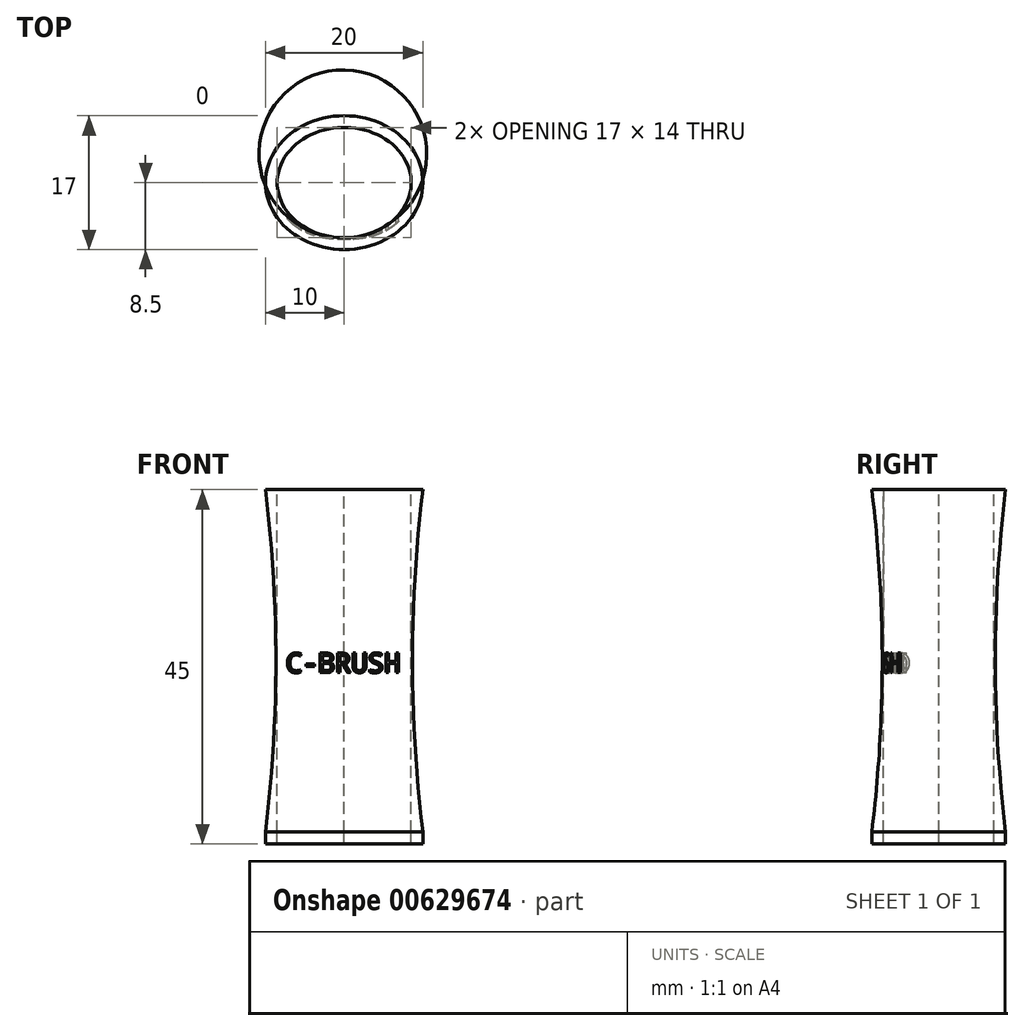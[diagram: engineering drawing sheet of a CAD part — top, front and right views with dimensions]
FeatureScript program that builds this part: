
annotation { "Feature Type Name" : "Feature", "Feature Type Description" : "" }
export const myFeature = defineFeature(function(context is Context, id is Id, definition is map)
    precondition{}
    {
        {
            var Q0;
            Q0=qCreatedBy(makeId("Top.planeOp"),FACE);
            var sketch = newSketch(context, id + "F0", { "sketchPlane" : qUnion([Q0])});
            skEllipse(sketch, "E0", {"center": v(0, 0) * mm, "majorRadius": 10 * mm, "minorRadius": 8.5 * mm, "majorAxis": v(-1, 0)});
            skSolve(sketch);
        }
        {
            var Q0;
            Q0 = qSketchRegion(id + "F0", true);
            extrude(context, id + "F1", {"entities" : qUnion([Q0]), "depth" : 1.5 * mm, "offsetDistance" : 25 * mm});
        }
        {
            var Q0;
            Q0=makeQuery(id+"F1.opExtrude","CAP_FACE",FACE,{"disambiguationData":[OSD([sQuery(id+"F0.wireOp",EDGE,"E0")])],"isStart":false});
            var sketch = newSketch(context, id + "F2", { "sketchPlane" : qUnion([Q0])});
            skSolve(sketch);
        }
        {
            var Q0;
            Q0=qCreatedBy(makeId("Top.planeOp"),FACE);
            cPlane(context, id + "F3", {"entities" : qUnion([Q0]), "cplaneType" : CPlaneType.OFFSET, "offset" : 45 * mm, "width" : 150 * mm, "height" : 150 * mm});
        }
        {
            var Q0;
            Q0=qCreatedBy(id+"F3.planeOp",FACE);
            var sketch = newSketch(context, id + "F4", { "sketchPlane" : qUnion([Q0])});
            skEllipse(sketch, "E1", {"center": v(0, 0) * mm, "majorRadius": 10 * mm, "minorRadius": 8.5 * mm, "majorAxis": v(-1, 0)});
            skSolve(sketch);
        }
        {
            var Q0;
            Q0=qCreatedBy(makeId("Front.planeOp"),FACE);
            var sketch = newSketch(context, id + "F5", { "sketchPlane" : qUnion([Q0])});
            skLineSegment(sketch, "E2", {"start": v(0, 0) * mm, "end": v(0, 1.5) * mm, "construction": true});
            skLineSegment(sketch, "E3", {"start": v(0, 1.5) * mm, "end": v(-10, 1.5) * mm, "construction": true});
            skLineSegment(sketch, "E4", {"start": v(0, 1.5) * mm, "end": v(10, 1.5) * mm, "construction": true});
            skLineSegment(sketch, "E5", {"start": v(-10, 1.5) * mm, "end": v(-10, 45) * mm, "construction": true});
            skLineSegment(sketch, "E6", {"start": v(10, 1.5) * mm, "end": v(10, 45) * mm, "construction": true});
            skArc(sketch, "E7", {"start": v(-10, 1.5) * mm, "mid": v(-8.68, 23.25) * mm, "end": v(-10, 45) * mm});
            skArc(sketch, "E8", {"start": v(10, 45) * mm, "mid": v(8.68, 23.25) * mm, "end": v(10, 1.5) * mm});
            skSolve(sketch);
        }
        {
            var Q0;
            Q0=qCreatedBy(makeId("Right.planeOp"),FACE);
            var sketch = newSketch(context, id + "F6", { "sketchPlane" : qUnion([Q0])});
            skLineSegment(sketch, "E9", {"start": v(0, 0) * mm, "end": v(0, 1.5) * mm, "construction": true});
            skLineSegment(sketch, "E10", {"start": v(0, 1.5) * mm, "end": v(8.5, 1.5) * mm, "construction": true});
            skLineSegment(sketch, "E11", {"start": v(8.5, 1.5) * mm, "end": v(8.5, 45) * mm, "construction": true});
            skLineSegment(sketch, "E12", {"start": v(0, 1.5) * mm, "end": v(-8.5, 1.5) * mm, "construction": true});
            skLineSegment(sketch, "E13", {"start": v(-8.5, 1.5) * mm, "end": v(-8.5, 45) * mm, "construction": true});
            skArc(sketch, "E14", {"start": v(-8.5, 1.5) * mm, "mid": v(-7.18, 23.25) * mm, "end": v(-8.5, 45) * mm});
            skArc(sketch, "E15", {"start": v(8.5, 45) * mm, "mid": v(7.18, 23.25) * mm, "end": v(8.5, 1.5) * mm});
            skSolve(sketch);
        }
        {
            var Q0;
            Q0=makeQuery(id+"F2.imprint","IMPRINT",FACE,{"disambiguationData":[TD([[makeQuery(id+"F2.imprint","IMPRINT",EDGE,{"derivedFrom":makeQuery(id+"F1.opExtrude","CAP_EDGE",EDGE,{"disambiguationData":[OSD([sQuery(id+"F0.wireOp",EDGE,"E0")])],"isStart":false})}),1.0]])]});
            var Q1;
            Q1 = qSketchRegion(id + "F4", true);
            var Q2;
            Q2=sQuery(id+"F5.wireOp",EDGE,"E7");
            var Q3;
            Q3=sQuery(id+"F5.wireOp",EDGE,"E8");
            var Q4;
            Q4=sQuery(id+"F6.wireOp",EDGE,"E14");
            var Q5;
            Q5=sQuery(id+"F6.wireOp",EDGE,"E15");
            loft(context, id + "F7", {"addGuides" : true, "sheetProfilesArray" : [{ "sheetProfileEntities" : qUnion([Q0]) }, { "sheetProfileEntities" : qUnion([Q1]) }], "guidesArray" : [{ "guideEntities" : qUnion([Q2]), "guideDerivativeType" : LoftGuideDerivativeType.DEFAULT, "guideDerivativeMagnitude" : 1 }, { "guideEntities" : qUnion([Q3]), "guideDerivativeType" : LoftGuideDerivativeType.DEFAULT, "guideDerivativeMagnitude" : 1 }, { "guideEntities" : qUnion([Q4]), "guideDerivativeType" : LoftGuideDerivativeType.DEFAULT, "guideDerivativeMagnitude" : 1 }, { "guideEntities" : qUnion([Q5]), "guideDerivativeType" : LoftGuideDerivativeType.DEFAULT, "guideDerivativeMagnitude" : 1 }]});
        }
        {
            var Q0;
            Q0=qCreatedBy(makeId("Front.planeOp"),FACE);
            var sketch = newSketch(context, id + "F8", { "sketchPlane" : qUnion([Q0])});
            skText(sketch, "E16", { "text": "C-BRUSH", "fontName": "DroidSansMono.ttf"});
            const initialGuessF8  = {"E16": [-0.00744, 0.02175, 1, 0, 0.0025]};
            skSetInitialGuess(sketch, initialGuessF8);
            skSolve(sketch);
        }
        {
            var Q0;
            Q0 = qSketchRegion(id + "F8", true);
            extrude(context, id + "F9", {"entities" : qUnion([Q0]), "operationType" : NewBodyOperationType.REMOVE, "endBound" : BoundingType.THROUGH_ALL, "depth" : 25 * mm, "offsetDistance" : 25 * mm});
        }
        {
            var Q0;
            Q0=makeQuery(id+"F7.opLoft","CAP_FACE",FACE,{"disambiguationData":[OSD([makeQuery(id+"F4.imprint","IMPRINT",FACE,{"disambiguationData":[TD([[makeQuery(id+"F4.imprint","IMPRINT",EDGE,{"derivedFrom":sQuery(id+"F4.wireOp",EDGE,"E1")}),1.0]])]})])],"isStart":true});
            var sketch = newSketch(context, id + "F10", { "sketchPlane" : qUnion([Q0])});
            skFitSpline(sketch, "E17.0", {"points": [v(-8.5, 0) * mm, v(-8.5, -0.22) * mm, v(-8.47, -0.66) * mm, v(-8.36, -1.32) * mm, v(-8.17, -1.97) * mm, v(-7.9, -2.6) * mm, v(-7.56, -3.21) * mm, v(-7.15, -3.8) * mm, v(-6.66, -4.36) * mm, v(-6.1, -4.88) * mm, v(-5.5, -5.35) * mm, v(-4.82, -5.77) * mm, v(-4.1, -6.14) * mm, v(-3.33, -6.45) * mm, v(-2.53, -6.7) * mm, v(-1.7, -6.87) * mm, v(-0.86, -6.98) * mm, v(-0.29, -7) * mm, v(0, -7) * mm]});
            skFitSpline(sketch, "E17.1", {"points": [v(0, 7) * mm, v(-0.29, 7) * mm, v(-0.86, 6.98) * mm, v(-1.7, 6.87) * mm, v(-2.53, 6.7) * mm, v(-3.33, 6.45) * mm, v(-4.1, 6.14) * mm, v(-4.82, 5.77) * mm, v(-5.5, 5.35) * mm, v(-6.11, 4.87) * mm, v(-6.66, 4.36) * mm, v(-7.15, 3.8) * mm, v(-7.56, 3.21) * mm, v(-7.9, 2.6) * mm, v(-8.17, 1.97) * mm, v(-8.36, 1.32) * mm, v(-8.47, 0.66) * mm, v(-8.5, 0.22) * mm, v(-8.5, 0) * mm]});
            skFitSpline(sketch, "E17.2", {"points": [v(8.5, 0) * mm, v(8.5, 0.22) * mm, v(8.47, 0.66) * mm, v(8.36, 1.32) * mm, v(8.17, 1.97) * mm, v(7.9, 2.6) * mm, v(7.56, 3.21) * mm, v(7.15, 3.8) * mm, v(6.66, 4.36) * mm, v(6.1, 4.88) * mm, v(5.5, 5.35) * mm, v(4.82, 5.77) * mm, v(4.1, 6.14) * mm, v(3.33, 6.45) * mm, v(2.53, 6.7) * mm, v(1.7, 6.87) * mm, v(0.86, 6.98) * mm, v(0.29, 7) * mm, v(0, 7) * mm]});
            skFitSpline(sketch, "E17.3", {"points": [v(0, -7) * mm, v(0.29, -7) * mm, v(0.86, -6.98) * mm, v(1.7, -6.87) * mm, v(2.53, -6.7) * mm, v(3.33, -6.45) * mm, v(4.1, -6.14) * mm, v(4.82, -5.77) * mm, v(5.5, -5.35) * mm, v(6.11, -4.87) * mm, v(6.66, -4.36) * mm, v(7.15, -3.8) * mm, v(7.56, -3.21) * mm, v(7.9, -2.6) * mm, v(8.17, -1.97) * mm, v(8.36, -1.32) * mm, v(8.47, -0.66) * mm, v(8.5, -0.22) * mm, v(8.5, 0) * mm]});
            skSolve(sketch);
        }
        {
            var Q0;
            Q0 = qSketchRegion(id + "F10", true);
            extrude(context, id + "F11", {"entities" : qUnion([Q0]), "operationType" : NewBodyOperationType.REMOVE, "endBound" : BoundingType.THROUGH_ALL, "oppositeDirection" : true, "depth" : 25 * mm, "offsetDistance" : 25 * mm});
        }
    });
